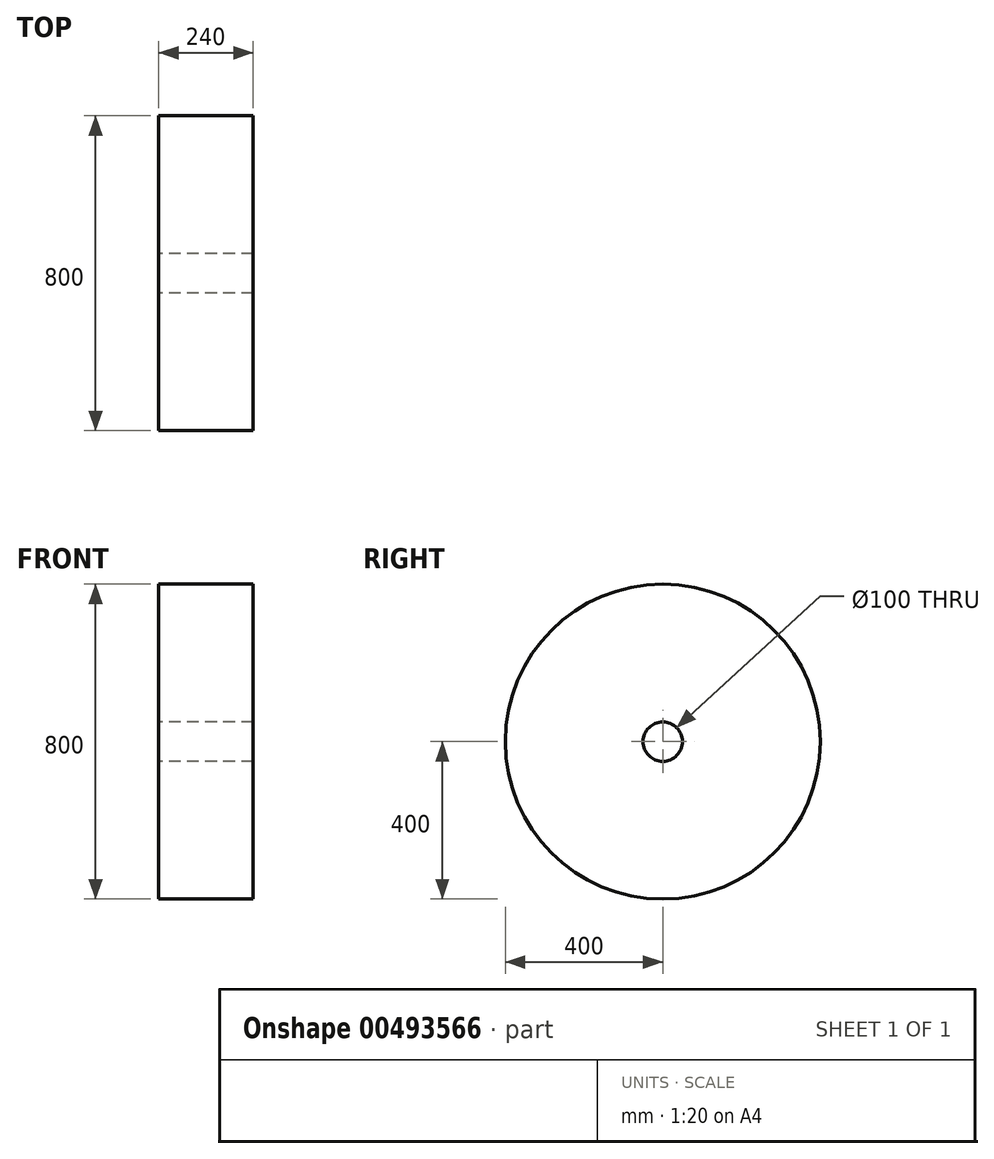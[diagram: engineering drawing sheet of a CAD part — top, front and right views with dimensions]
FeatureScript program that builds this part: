
annotation { "Feature Type Name" : "Feature", "Feature Type Description" : "" }
export const myFeature = defineFeature(function(context is Context, id is Id, definition is map)
    precondition{}
    {
        {
            var Q0;
            Q0=qCreatedBy(makeId("Front.planeOp"),FACE);
            var sketch = newSketch(context, id + "F0", { "sketchPlane" : qUnion([Q0])});
            skLineSegment(sketch, "E0.bottom", {"start": v(-120, 400) * mm, "end": v(120, 400) * mm});
            skLineSegment(sketch, "E0.top", {"start": v(-120, 50) * mm, "end": v(120, 50) * mm});
            skLineSegment(sketch, "E0.left", {"start": v(-120, 400) * mm, "end": v(-120, 50) * mm});
            skLineSegment(sketch, "E0.right", {"start": v(120, 400) * mm, "end": v(120, 50) * mm});
            skLineSegment(sketch, "E1", {"start": v(-121.99, 0) * mm, "end": v(128.53, 0) * mm, "construction": true});
            skSolve(sketch);
        }
        {
            var Q0;
            Q0=makeQuery(id+"F0.imprint","IMPRINT",FACE,{"disambiguationData":[TD([[makeQuery(id+"F0.imprint","IMPRINT",EDGE,{"derivedFrom":sQuery(id+"F0.wireOp",EDGE,"E0.bottom")}),-1.0]])]});
            var Q1;
            Q1=sQuery(id+"F0.wireOp",EDGE,"E1");
            revolve(context, id + "F1", {"entities" : qUnion([Q0]), "axis" : qUnion([Q1]), "revolveType" : RevolveType.FULL});
        }
    });
